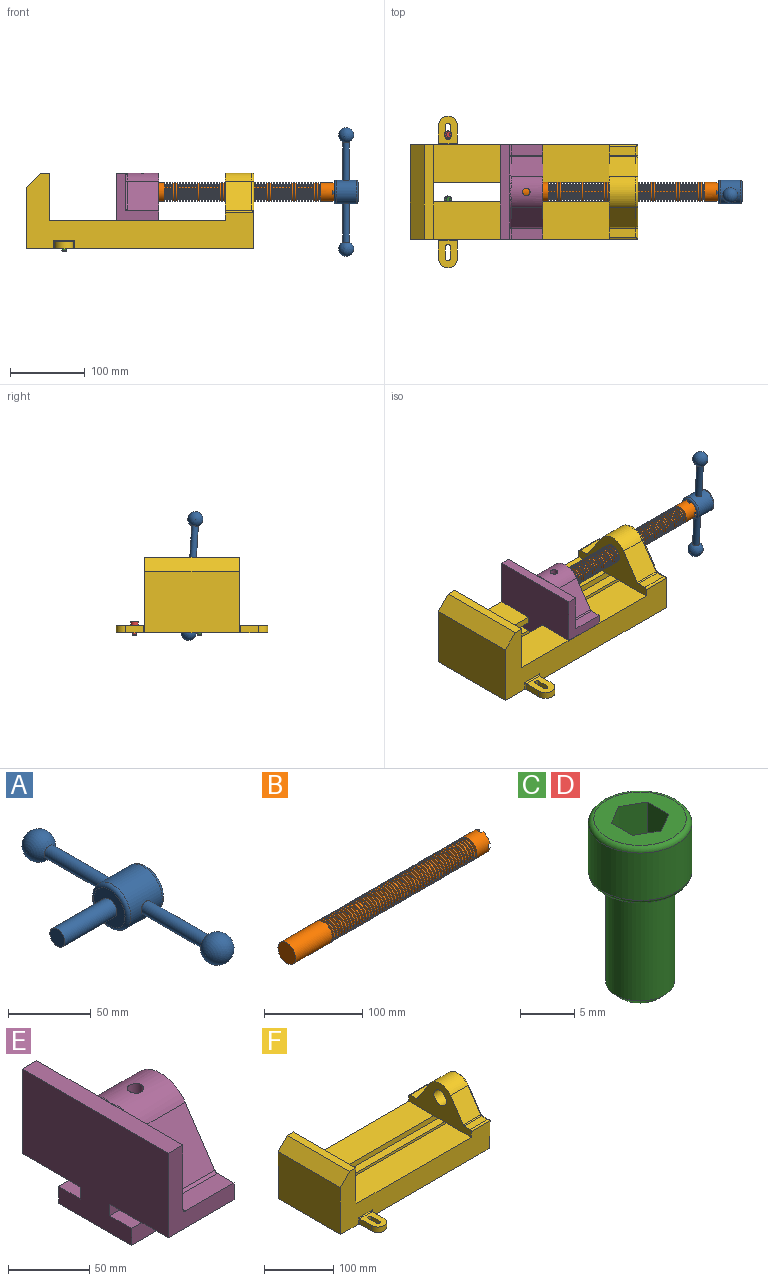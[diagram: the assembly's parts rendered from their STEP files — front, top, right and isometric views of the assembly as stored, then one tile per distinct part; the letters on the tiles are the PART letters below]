
ASSEMBLY  parts=6 mates=7
PART A: 11 faces, bbox 76.2x172.7x34.4 mm
  f0: sphere r=10.16mm, area 1231.8mm2, adj f1
  f1: cylinder r=4.45mm len=51.82mm, axis (0,1,0), area 1438.5mm2, adj f0,f4
  f2: sphere r=10.16mm, area 1231.8mm2, adj f3
  f3: cylinder r=4.45mm len=51.82mm, axis (0,1,0), area 1438.5mm2, adj f2,f4
  f4: cylinder r=15.88mm len=31.75mm, axis (-1,0,0), area 2534.7mm2, adj f1,f3,f9,f10
  f5: cylinder r=6.35mm len=44.45mm, axis (-1,0,0), area 1773.5mm2, adj f6,f8
  f6: plane 12.7x12.7mm, normal (-1,0,0), area 126.7mm2, adj f5
  f7: plane 26.67x26.67mm, normal (1,0,0), area 558.6mm2, adj f10
  f8: plane 26.67x26.67mm, normal (-1,0,0), area 432mm2, adj f5,f9
  f9: torus R=13.33mm, axis (1,0,0), area 374.8mm2, adj f4,f8
  f10: torus R=13.33mm, axis (1,0,0), area 374.8mm2, adj f4,f7
PART B: 220 faces, bbox 279.4x25.4x25.4 mm
  f0: cylinder r=12.7mm len=25.4mm, axis (-1,0,0), area 1468.2mm2, adj f1,f2,f3,f5,f7,f208,f209,f210
  f1: plane 9.9x9.9mm, normal (1,0,0), area 62.3mm2, adj f0,f4,f213,f216
  f2: plane 9.9x9.9mm, normal (1,0,0), area 62.3mm2, adj f0,f4,f210,f218
  f3: plane 9.9x9.9mm, normal (1,0,0), area 62.3mm2, adj f0,f4,f209,f212
  f4: cylinder r=6.35mm len=25.4mm, axis (1,0,0), area 960.3mm2, adj f1,f2,f3,f5,f6,f208,f209,f210
  f5: plane 9.9x9.9mm, normal (1,0,0), area 62.3mm2, adj f0,f4,f215,f217
  f6: plane 12.7x12.7mm, normal (1,0,0), area 126.7mm2, adj f4
  f7: cone r=12.7mm half-angle=76deg, axis (1,0,0), area 188mm2, adj f0,f9
  f8: cone r=10.16mm half-angle=76deg, axis (-1,0,0), area 188mm2, adj f9,f10
  f9: cylinder r=10.16mm len=20.32mm, axis (1,0,0), area 81.1mm2, adj f7,f8
  f10: cylinder r=12.7mm len=25.4mm, axis (-1,0,0), area 131.7mm2, adj f8,f11
  f11: cone r=12.7mm half-angle=76deg, axis (1,0,0), area 188mm2, adj f10,f13
  f12: cone r=10.16mm half-angle=76deg, axis (-1,0,0), area 188mm2, adj f13,f14
  f13: cylinder r=10.16mm len=20.32mm, axis (1,0,0), area 81.1mm2, adj f11,f12
  f14: cylinder r=12.7mm len=25.4mm, axis (-1,0,0), area 131.7mm2, adj f12,f15
  f15: cone r=12.7mm half-angle=76deg, axis (1,0,0), area 188mm2, adj f14,f17
  f16: cone r=10.16mm half-angle=76deg, axis (-1,0,0), area 188mm2, adj f17,f18
  f17: cylinder r=10.16mm len=20.32mm, axis (1,0,0), area 81.1mm2, adj f15,f16
  f18: cylinder r=12.7mm len=25.4mm, axis (-1,0,0), area 131.7mm2, adj f16,f19
  f19: cone r=12.7mm half-angle=76deg, axis (1,0,0), area 188mm2, adj f18,f21
  f20: cone r=10.16mm half-angle=76deg, axis (-1,0,0), area 188mm2, adj f21,f22
  f21: cylinder r=10.16mm len=20.32mm, axis (1,0,0), area 81.1mm2, adj f19,f20
  f22: cylinder r=12.7mm len=25.4mm, axis (-1,0,0), area 131.7mm2, adj f20,f23
  f23: cone r=12.7mm half-angle=76deg, axis (1,0,0), area 188mm2, adj f22,f25
  f24: cone r=10.16mm half-angle=76deg, axis (-1,0,0), area 188mm2, adj f25,f26
  f25: cylinder r=10.16mm len=20.32mm, axis (1,0,0), area 81.1mm2, adj f23,f24
  f26: cylinder r=12.7mm len=25.4mm, axis (-1,0,0), area 131.7mm2, adj f24,f27
  f27: cone r=12.7mm half-angle=76deg, axis (1,0,0), area 188mm2, adj f26,f29
  f28: cone r=10.16mm half-angle=76deg, axis (-1,0,0), area 188mm2, adj f29,f30
  f29: cylinder r=10.16mm len=20.32mm, axis (1,0,0), area 81.1mm2, adj f27,f28
  f30: cylinder r=12.7mm len=25.4mm, axis (-1,0,0), area 131.7mm2, adj f28,f31
  f31: cone r=12.7mm half-angle=76deg, axis (1,0,0), area 188mm2, adj f30,f33
  f32: cone r=10.16mm half-angle=76deg, axis (-1,0,0), area 188mm2, adj f33,f34
  f33: cylinder r=10.16mm len=20.32mm, axis (1,0,0), area 81.1mm2, adj f31,f32
  f34: cylinder r=12.7mm len=25.4mm, axis (-1,0,0), area 131.7mm2, adj f32,f35
  f35: cone r=12.7mm half-angle=76deg, axis (1,0,0), area 188mm2, adj f34,f37
  f36: cone r=10.16mm half-angle=76deg, axis (-1,0,0), area 188mm2, adj f37,f38
  f37: cylinder r=10.16mm len=20.32mm, axis (1,0,0), area 81.1mm2, adj f35,f36
  f38: cylinder r=12.7mm len=25.4mm, axis (-1,0,0), area 131.7mm2, adj f36,f39
  f39: cone r=12.7mm half-angle=76deg, axis (1,0,0), area 188mm2, adj f38,f41
  f40: cone r=10.16mm half-angle=76deg, axis (-1,0,0), area 188mm2, adj f41,f42
  f41: cylinder r=10.16mm len=20.32mm, axis (1,0,0), area 81.1mm2, adj f39,f40
  f42: cylinder r=12.7mm len=25.4mm, axis (-1,0,0), area 131.7mm2, adj f40,f43
  f43: cone r=12.7mm half-angle=76deg, axis (1,0,0), area 188mm2, adj f42,f45
  f44: cone r=10.16mm half-angle=76deg, axis (-1,0,0), area 188mm2, adj f45,f46
  f45: cylinder r=10.16mm len=20.32mm, axis (1,0,0), area 81.1mm2, adj f43,f44
  f46: cylinder r=12.7mm len=25.4mm, axis (-1,0,0), area 131.7mm2, adj f44,f47
  f47: cone r=12.7mm half-angle=76deg, axis (1,0,0), area 188mm2, adj f46,f49
  f48: cone r=10.16mm half-angle=76deg, axis (-1,0,0), area 188mm2, adj f49,f50
  f49: cylinder r=10.16mm len=20.32mm, axis (1,0,0), area 81.1mm2, adj f47,f48
  f50: cylinder r=12.7mm len=25.4mm, axis (-1,0,0), area 131.7mm2, adj f48,f51
  f51: cone r=12.7mm half-angle=76deg, axis (1,0,0), area 188mm2, adj f50,f53
  f52: cone r=10.16mm half-angle=76deg, axis (-1,0,0), area 188mm2, adj f53,f54
  f53: cylinder r=10.16mm len=20.32mm, axis (1,0,0), area 81.1mm2, adj f51,f52
  f54: cylinder r=12.7mm len=25.4mm, axis (-1,0,0), area 131.7mm2, adj f52,f55
  f55: cone r=12.7mm half-angle=76deg, axis (1,0,0), area 188mm2, adj f54,f57
  f56: cone r=10.16mm half-angle=76deg, axis (-1,0,0), area 188mm2, adj f57,f58
  f57: cylinder r=10.16mm len=20.32mm, axis (1,0,0), area 81.1mm2, adj f55,f56
  f58: cylinder r=12.7mm len=25.4mm, axis (-1,0,0), area 131.7mm2, adj f56,f59
  f59: cone r=12.7mm half-angle=76deg, axis (1,0,0), area 188mm2, adj f58,f61
  f60: cone r=10.16mm half-angle=76deg, axis (-1,0,0), area 188mm2, adj f61,f62
  f61: cylinder r=10.16mm len=20.32mm, axis (1,0,0), area 81.1mm2, adj f59,f60
  f62: cylinder r=12.7mm len=25.4mm, axis (-1,0,0), area 131.7mm2, adj f60,f63
  f63: cone r=12.7mm half-angle=76deg, axis (1,0,0), area 188mm2, adj f62,f65
  f64: cone r=10.16mm half-angle=76deg, axis (-1,0,0), area 188mm2, adj f65,f66
  f65: cylinder r=10.16mm len=20.32mm, axis (1,0,0), area 81.1mm2, adj f63,f64
  f66: cylinder r=12.7mm len=25.4mm, axis (-1,0,0), area 131.7mm2, adj f64,f67
  f67: cone r=12.7mm half-angle=76deg, axis (1,0,0), area 188mm2, adj f66,f69
  f68: cone r=10.16mm half-angle=76deg, axis (-1,0,0), area 188mm2, adj f69,f70
  f69: cylinder r=10.16mm len=20.32mm, axis (1,0,0), area 81.1mm2, adj f67,f68
  f70: cylinder r=12.7mm len=25.4mm, axis (-1,0,0), area 131.7mm2, adj f68,f71
  f71: cone r=12.7mm half-angle=76deg, axis (1,0,0), area 188mm2, adj f70,f73
  f72: cone r=10.16mm half-angle=76deg, axis (-1,0,0), area 188mm2, adj f73,f74
  f73: cylinder r=10.16mm len=20.32mm, axis (1,0,0), area 81.1mm2, adj f71,f72
  f74: cylinder r=12.7mm len=25.4mm, axis (-1,0,0), area 131.7mm2, adj f72,f75
  f75: cone r=12.7mm half-angle=76deg, axis (1,0,0), area 188mm2, adj f74,f77
  f76: cone r=10.16mm half-angle=76deg, axis (-1,0,0), area 188mm2, adj f77,f78
  f77: cylinder r=10.16mm len=20.32mm, axis (1,0,0), area 81.1mm2, adj f75,f76
  f78: cylinder r=12.7mm len=25.4mm, axis (-1,0,0), area 131.7mm2, adj f76,f79
  f79: cone r=12.7mm half-angle=76deg, axis (1,0,0), area 188mm2, adj f78,f81
  f80: cone r=10.16mm half-angle=76deg, axis (-1,0,0), area 188mm2, adj f81,f82
  f81: cylinder r=10.16mm len=20.32mm, axis (1,0,0), area 81.1mm2, adj f79,f80
  f82: cylinder r=12.7mm len=25.4mm, axis (-1,0,0), area 131.7mm2, adj f80,f83
  f83: cone r=12.7mm half-angle=76deg, axis (1,0,0), area 188mm2, adj f82,f85
  f84: cone r=10.16mm half-angle=76deg, axis (-1,0,0), area 188mm2, adj f85,f86
  f85: cylinder r=10.16mm len=20.32mm, axis (1,0,0), area 81.1mm2, adj f83,f84
  f86: cylinder r=12.7mm len=25.4mm, axis (-1,0,0), area 131.7mm2, adj f84,f87
  f87: cone r=12.7mm half-angle=76deg, axis (1,0,0), area 188mm2, adj f86,f89
  f88: cone r=10.16mm half-angle=76deg, axis (-1,0,0), area 188mm2, adj f89,f90
  f89: cylinder r=10.16mm len=20.32mm, axis (1,0,0), area 81.1mm2, adj f87,f88
  f90: cylinder r=12.7mm len=25.4mm, axis (-1,0,0), area 131.7mm2, adj f88,f91
  f91: cone r=12.7mm half-angle=76deg, axis (1,0,0), area 188mm2, adj f90,f93
  f92: cone r=10.16mm half-angle=76deg, axis (-1,0,0), area 188mm2, adj f93,f94
  f93: cylinder r=10.16mm len=20.32mm, axis (1,0,0), area 81.1mm2, adj f91,f92
  f94: cylinder r=12.7mm len=25.4mm, axis (-1,0,0), area 131.7mm2, adj f92,f95
  f95: cone r=12.7mm half-angle=76deg, axis (1,0,0), area 188mm2, adj f94,f97
  f96: cone r=10.16mm half-angle=76deg, axis (-1,0,0), area 188mm2, adj f97,f98
  f97: cylinder r=10.16mm len=20.32mm, axis (1,0,0), area 81.1mm2, adj f95,f96
  f98: cylinder r=12.7mm len=25.4mm, axis (-1,0,0), area 131.7mm2, adj f96,f99
  f99: cone r=12.7mm half-angle=76deg, axis (1,0,0), area 188mm2, adj f98,f101
  f100: cone r=10.16mm half-angle=76deg, axis (-1,0,0), area 188mm2, adj f101,f102
  f101: cylinder r=10.16mm len=20.32mm, axis (1,0,0), area 81.1mm2, adj f99,f100
  f102: cylinder r=12.7mm len=25.4mm, axis (-1,0,0), area 131.7mm2, adj f100,f103
  f103: cone r=12.7mm half-angle=76deg, axis (1,0,0), area 188mm2, adj f102,f105
  f104: cone r=10.16mm half-angle=76deg, axis (-1,0,0), area 188mm2, adj f105,f106
  f105: cylinder r=10.16mm len=20.32mm, axis (1,0,0), area 81.1mm2, adj f103,f104
  f106: cylinder r=12.7mm len=25.4mm, axis (-1,0,0), area 131.7mm2, adj f104,f107
  f107: cone r=12.7mm half-angle=76deg, axis (1,0,0), area 188mm2, adj f106,f109
  f108: cone r=10.16mm half-angle=76deg, axis (-1,0,0), area 188mm2, adj f109,f110
  f109: cylinder r=10.16mm len=20.32mm, axis (1,0,0), area 81.1mm2, adj f107,f108
  f110: cylinder r=12.7mm len=25.4mm, axis (-1,0,0), area 131.7mm2, adj f108,f111
  f111: cone r=12.7mm half-angle=76deg, axis (1,0,0), area 188mm2, adj f110,f113
  f112: cone r=10.16mm half-angle=76deg, axis (-1,0,0), area 188mm2, adj f113,f114
  f113: cylinder r=10.16mm len=20.32mm, axis (1,0,0), area 81.1mm2, adj f111,f112
  f114: cylinder r=12.7mm len=25.4mm, axis (-1,0,0), area 131.7mm2, adj f112,f115
  f115: cone r=12.7mm half-angle=76deg, axis (1,0,0), area 188mm2, adj f114,f117
  f116: cone r=10.16mm half-angle=76deg, axis (-1,0,0), area 188mm2, adj f117,f118
  f117: cylinder r=10.16mm len=20.32mm, axis (1,0,0), area 81.1mm2, adj f115,f116
  f118: cylinder r=12.7mm len=25.4mm, axis (-1,0,0), area 131.7mm2, adj f116,f119
  f119: cone r=12.7mm half-angle=76deg, axis (1,0,0), area 188mm2, adj f118,f121
  f120: cone r=10.16mm half-angle=76deg, axis (-1,0,0), area 188mm2, adj f121,f122
  f121: cylinder r=10.16mm len=20.32mm, axis (1,0,0), area 81.1mm2, adj f119,f120
  f122: cylinder r=12.7mm len=25.4mm, axis (-1,0,0), area 131.7mm2, adj f120,f123
  f123: cone r=12.7mm half-angle=76deg, axis (1,0,0), area 188mm2, adj f122,f125
  f124: cone r=10.16mm half-angle=76deg, axis (-1,0,0), area 188mm2, adj f125,f126
  f125: cylinder r=10.16mm len=20.32mm, axis (1,0,0), area 81.1mm2, adj f123,f124
  f126: cylinder r=12.7mm len=25.4mm, axis (-1,0,0), area 131.7mm2, adj f124,f127
  f127: cone r=12.7mm half-angle=76deg, axis (1,0,0), area 188mm2, adj f126,f129
  f128: cone r=10.16mm half-angle=76deg, axis (-1,0,0), area 188mm2, adj f129,f130
  f129: cylinder r=10.16mm len=20.32mm, axis (1,0,0), area 81.1mm2, adj f127,f128
  f130: cylinder r=12.7mm len=25.4mm, axis (-1,0,0), area 131.7mm2, adj f128,f131
  f131: cone r=12.7mm half-angle=76deg, axis (1,0,0), area 188mm2, adj f130,f133
  f132: cone r=10.16mm half-angle=76deg, axis (-1,0,0), area 188mm2, adj f133,f134
  f133: cylinder r=10.16mm len=20.32mm, axis (1,0,0), area 81.1mm2, adj f131,f132
  f134: cylinder r=12.7mm len=25.4mm, axis (-1,0,0), area 131.7mm2, adj f132,f135
  f135: cone r=12.7mm half-angle=76deg, axis (1,0,0), area 188mm2, adj f134,f137
  f136: cone r=10.16mm half-angle=76deg, axis (-1,0,0), area 188mm2, adj f137,f138
  f137: cylinder r=10.16mm len=20.32mm, axis (1,0,0), area 81.1mm2, adj f135,f136
  f138: cylinder r=12.7mm len=25.4mm, axis (-1,0,0), area 131.7mm2, adj f136,f139
  f139: cone r=12.7mm half-angle=76deg, axis (1,0,0), area 188mm2, adj f138,f141
  f140: cone r=10.16mm half-angle=76deg, axis (-1,0,0), area 188mm2, adj f141,f142
  f141: cylinder r=10.16mm len=20.32mm, axis (1,0,0), area 81.1mm2, adj f139,f140
  f142: cylinder r=12.7mm len=25.4mm, axis (-1,0,0), area 131.7mm2, adj f140,f143
  f143: cone r=12.7mm half-angle=76deg, axis (1,0,0), area 188mm2, adj f142,f145
  f144: cone r=10.16mm half-angle=76deg, axis (-1,0,0), area 188mm2, adj f145,f146
  f145: cylinder r=10.16mm len=20.32mm, axis (1,0,0), area 81.1mm2, adj f143,f144
  f146: cylinder r=12.7mm len=25.4mm, axis (-1,0,0), area 131.7mm2, adj f144,f147
  f147: cone r=12.7mm half-angle=76deg, axis (1,0,0), area 188mm2, adj f146,f149
  f148: cone r=10.16mm half-angle=76deg, axis (-1,0,0), area 188mm2, adj f149,f150
  f149: cylinder r=10.16mm len=20.32mm, axis (1,0,0), area 81.1mm2, adj f147,f148
  f150: cylinder r=12.7mm len=25.4mm, axis (-1,0,0), area 131.7mm2, adj f148,f151
  f151: cone r=12.7mm half-angle=76deg, axis (1,0,0), area 188mm2, adj f150,f153
  f152: cone r=10.16mm half-angle=76deg, axis (-1,0,0), area 188mm2, adj f153,f154
  f153: cylinder r=10.16mm len=20.32mm, axis (1,0,0), area 81.1mm2, adj f151,f152
  f154: cylinder r=12.7mm len=25.4mm, axis (-1,0,0), area 131.7mm2, adj f152,f155
  f155: cone r=12.7mm half-angle=76deg, axis (1,0,0), area 188mm2, adj f154,f157
  f156: cone r=10.16mm half-angle=76deg, axis (-1,0,0), area 188mm2, adj f157,f158
  f157: cylinder r=10.16mm len=20.32mm, axis (1,0,0), area 81.1mm2, adj f155,f156
  f158: cylinder r=12.7mm len=25.4mm, axis (-1,0,0), area 131.7mm2, adj f156,f159
  f159: cone r=12.7mm half-angle=76deg, axis (1,0,0), area 188mm2, adj f158,f161
  f160: cone r=10.16mm half-angle=76deg, axis (-1,0,0), area 188mm2, adj f161,f162
  f161: cylinder r=10.16mm len=20.32mm, axis (1,0,0), area 81.1mm2, adj f159,f160
  f162: cylinder r=12.7mm len=25.4mm, axis (-1,0,0), area 131.7mm2, adj f160,f163
  f163: cone r=12.7mm half-angle=76deg, axis (1,0,0), area 188mm2, adj f162,f165
  f164: cone r=10.16mm half-angle=76deg, axis (-1,0,0), area 188mm2, adj f165,f166
  f165: cylinder r=10.16mm len=20.32mm, axis (1,0,0), area 81.1mm2, adj f163,f164
  f166: cylinder r=12.7mm len=25.4mm, axis (-1,0,0), area 131.7mm2, adj f164,f167
  f167: cone r=12.7mm half-angle=76deg, axis (1,0,0), area 188mm2, adj f166,f169
  f168: cone r=10.16mm half-angle=76deg, axis (-1,0,0), area 188mm2, adj f169,f170
  f169: cylinder r=10.16mm len=20.32mm, axis (1,0,0), area 81.1mm2, adj f167,f168
  f170: cylinder r=12.7mm len=25.4mm, axis (-1,0,0), area 131.7mm2, adj f168,f171
  f171: cone r=12.7mm half-angle=76deg, axis (1,0,0), area 188mm2, adj f170,f173
  f172: cone r=10.16mm half-angle=76deg, axis (-1,0,0), area 188mm2, adj f173,f174
  f173: cylinder r=10.16mm len=20.32mm, axis (1,0,0), area 81.1mm2, adj f171,f172
  f174: cylinder r=12.7mm len=25.4mm, axis (-1,0,0), area 131.7mm2, adj f172,f175
  f175: cone r=12.7mm half-angle=76deg, axis (1,0,0), area 188mm2, adj f174,f177
  f176: cone r=10.16mm half-angle=76deg, axis (-1,0,0), area 188mm2, adj f177,f178
  f177: cylinder r=10.16mm len=20.32mm, axis (1,0,0), area 81.1mm2, adj f175,f176
  f178: cylinder r=12.7mm len=25.4mm, axis (-1,0,0), area 131.7mm2, adj f176,f179
  f179: cone r=12.7mm half-angle=76deg, axis (1,0,0), area 188mm2, adj f178,f181
  f180: cone r=10.16mm half-angle=76deg, axis (-1,0,0), area 188mm2, adj f181,f182
  f181: cylinder r=10.16mm len=20.32mm, axis (1,0,0), area 81.1mm2, adj f179,f180
  f182: cylinder r=12.7mm len=25.4mm, axis (-1,0,0), area 131.7mm2, adj f180,f183
  f183: cone r=12.7mm half-angle=76deg, axis (1,0,0), area 188mm2, adj f182,f185
  f184: cone r=10.16mm half-angle=76deg, axis (-1,0,0), area 188mm2, adj f185,f186
  f185: cylinder r=10.16mm len=20.32mm, axis (1,0,0), area 81.1mm2, adj f183,f184
  f186: cylinder r=12.7mm len=25.4mm, axis (-1,0,0), area 131.7mm2, adj f184,f187
  f187: cone r=12.7mm half-angle=76deg, axis (1,0,0), area 188mm2, adj f186,f189
  f188: cone r=10.16mm half-angle=76deg, axis (-1,0,0), area 188mm2, adj f189,f190
  f189: cylinder r=10.16mm len=20.32mm, axis (1,0,0), area 81.1mm2, adj f187,f188
  f190: cylinder r=12.7mm len=25.4mm, axis (-1,0,0), area 131.7mm2, adj f188,f191
  f191: cone r=12.7mm half-angle=76deg, axis (1,0,0), area 188mm2, adj f190,f193
  f192: cone r=10.16mm half-angle=76deg, axis (-1,0,0), area 188mm2, adj f193,f194
  f193: cylinder r=10.16mm len=20.32mm, axis (1,0,0), area 81.1mm2, adj f191,f192
  f194: cylinder r=12.7mm len=25.4mm, axis (-1,0,0), area 131.7mm2, adj f192,f195
  f195: cone r=12.7mm half-angle=76deg, axis (1,0,0), area 188mm2, adj f194,f197
  f196: cone r=10.16mm half-angle=76deg, axis (-1,0,0), area 188mm2, adj f197,f198
  f197: cylinder r=10.16mm len=20.32mm, axis (1,0,0), area 81.1mm2, adj f195,f196
  f198: cylinder r=12.7mm len=25.4mm, axis (-1,0,0), area 131.7mm2, adj f196,f199
  f199: cone r=12.7mm half-angle=76deg, axis (1,0,0), area 188mm2, adj f198,f201
  f200: cone r=10.16mm half-angle=76deg, axis (-1,0,0), area 188mm2, adj f201,f202
  f201: cylinder r=10.16mm len=20.32mm, axis (1,0,0), area 81.1mm2, adj f199,f200
  f202: cylinder r=12.7mm len=25.4mm, axis (-1,0,0), area 131.7mm2, adj f200,f203
  f203: cone r=12.7mm half-angle=76deg, axis (1,0,0), area 188mm2, adj f202,f205
  f204: cone r=10.16mm half-angle=76deg, axis (-1,0,0), area 188mm2, adj f205,f207
  f205: cylinder r=10.16mm len=20.32mm, axis (1,0,0), area 81.1mm2, adj f203,f204
  f206: plane 25.4x25.4mm, normal (-1,0,0), area 506.7mm2, adj f207
  f207: cylinder r=12.7mm len=52.45mm, axis (-1,0,0), area 4185.4mm2, adj f204,f206
  f208: plane 6.88x5.08mm, normal (1,0,0), area 32.7mm2, adj f0,f4,f209,f210
  f209: plane 6.62x2.54mm, normal (0,-1,0), area 16.8mm2, adj f0,f3,f4,f208
  f210: plane 6.62x2.54mm, normal (0,1,0), area 16.8mm2, adj f0,f2,f4,f208
  f211: plane 6.88x5.08mm, normal (1,0,0), area 32.7mm2, adj f0,f4,f212,f213
  f212: plane 6.62x2.54mm, normal (0,0,1), area 16.8mm2, adj f0,f3,f4,f211
  f213: plane 6.62x2.54mm, normal (0,0,-1), area 16.8mm2, adj f0,f1,f4,f211
  f214: plane 6.88x5.08mm, normal (1,0,0), area 32.7mm2, adj f0,f4,f215,f216
  f215: plane 6.62x2.54mm, normal (0,1,0), area 16.8mm2, adj f0,f4,f5,f214
  f216: plane 6.62x2.54mm, normal (0,-1,0), area 16.8mm2, adj f0,f1,f4,f214
  f217: plane 6.62x2.54mm, normal (0,0,-1), area 16.8mm2, adj f0,f4,f5,f219
  f218: plane 6.62x2.54mm, normal (0,0,1), area 16.8mm2, adj f0,f2,f4,f219
  f219: plane 6.88x5.08mm, normal (1,0,0), area 32.7mm2, adj f0,f4,f217,f218
PART C: 15 faces, bbox 10.3x10.3x19.1 mm
  f0: plane 8.51x8.51mm, normal (0,0,1), area 37.2mm2, adj f5,f6,f7,f8,f9,f10,f14
  f1: cylinder r=3.17mm len=11.94mm, axis (0,0,1), area 238.2mm2, adj f4,f12
  f2: plane 4.83x4.83mm, normal (0,0,-1), area 18.3mm2, adj f12
  f3: cylinder r=4.76mm len=9.53mm, axis (0,0,-1), area 159.6mm2, adj f13,f14
  f4: plane 8.51x8.51mm, normal (0,0,-1), area 25.2mm2, adj f1,f13
  f5: plane 4.83x2.38mm, normal (-0.5,-0.87,0), area 13.3mm2, adj f0,f6,f10,f11
  f6: plane 4.83x2.38mm, normal (0.5,-0.87,0), area 13.3mm2, adj f0,f5,f7,f11
  f7: plane 4.83x2.75mm, normal (1,0,0), area 13.3mm2, adj f0,f6,f8,f11
  f8: plane 4.83x2.38mm, normal (0.5,0.87,0), area 13.3mm2, adj f0,f7,f9,f11
  f9: plane 4.83x2.38mm, normal (-0.5,0.87,0), area 13.3mm2, adj f0,f8,f10,f11
  f10: plane 4.83x2.75mm, normal (-1,0,0), area 13.3mm2, adj f0,f5,f9,f11
  f11: plane 5.5x4.76mm, normal (0,0,1), area 19.6mm2, adj f5,f6,f7,f8,f9,f10
  f12: cone r=3.17mm half-angle=45deg, axis (0,0,1), area 18.9mm2, adj f1,f2
  f13: torus R=4.25mm, axis (0,0,1), area 23mm2, adj f3,f4
  f14: torus R=4.25mm, axis (0,0,1), area 23mm2, adj f0,f3
PART D: same geometry as C
PART E: 36 faces, bbox 57.2x127x89 mm
  f0: plane 57.15x50.8mm, normal (0,0,-1), area 2903.2mm2, adj f6,f9,f10,f23
  f1: cylinder r=12.7mm len=44.45mm, axis (1,0,0), area 3464.3mm2, adj f6,f15,f16
  f2: plane 41.91x14.52mm, normal (0,0,1), area 608.5mm2, adj f6,f11,f24,f25
  f3: plane 51.86x48.26mm, normal (1,0,0), area 1495.7mm2, adj f8,f10,f31,f33,f35
  f4: plane 51.86x48.26mm, normal (1,0,0), area 1495.7mm2, adj f8,f11,f24,f28,f29
  f5: plane 57.15x50.8mm, normal (0,0,-1), area 2903.2mm2, adj f6,f9,f11,f22
  f6: plane 127x85.09mm, normal (1,0,0), area 5190.6mm2, adj f0,f1,f2,f5,f7,f10,f11,f12
  f7: plane 41.91x14.52mm, normal (0,0,1), area 608.5mm2, adj f6,f10,f30,f31
  f8: plane 127x12.7mm, normal (0,0,1), area 1612.9mm2, adj f3,f4,f9,f10,f11,f26,f34
  f9: plane 127x85.09mm, normal (-1,0,0), area 9096.8mm2, adj f0,f5,f8,f10,f11,f17,f18,f19
  f10: plane 63.5x57.15mm, normal (0,-1,0), area 1372.3mm2, adj f0,f3,f6,f7,f8,f9,f31
  f11: plane 63.5x57.15mm, normal (0,1,0), area 1372.3mm2, adj f2,f4,f5,f6,f8,f9,f24
  f12: plane 41.91x38.43mm, normal (0,-0.83,0.56), area 1939.2mm2, adj f6,f13,f30,f33
  f13: cylinder r=25.4mm len=44.45mm, axis (1,0,0), area 2026.5mm2, adj f6,f12,f14,f16,f26,f28,f34,f35
  f14: plane 41.91x38.43mm, normal (0,0.83,0.56), area 1939.2mm2, adj f6,f13,f25,f29
  f15: plane 25.4x25.4mm, normal (1,0,0), area 506.7mm2, adj f1
  f16: cylinder r=5.08mm len=13.76mm, axis (0,0,1), area 414mm2, adj f1,f13
  f17: plane 57.15x19.05mm, normal (0,0,1), area 1088.7mm2, adj f6,f9,f18,f23
  f18: plane 57.15x12.7mm, normal (0,-1,0), area 725.8mm2, adj f6,f9,f17,f19
  f19: plane 63.5x57.15mm, normal (0,0,-1), area 3629mm2, adj f6,f9,f18,f20
  f20: plane 57.15x12.7mm, normal (0,1,0), area 725.8mm2, adj f6,f9,f19,f21
  f21: plane 57.15x19.05mm, normal (0,0,1), area 1088.7mm2, adj f6,f9,f20,f22
  f22: plane 57.15x8.89mm, normal (0,1,0), area 508.1mm2, adj f5,f6,f9,f21
  f23: plane 57.15x8.89mm, normal (0,-1,0), area 508.1mm2, adj f0,f6,f9,f17
  f24: cylinder r=2.54mm len=14.52mm, axis (0,-1,0), area 57.9mm2, adj f2,f4,f11,f27
  f25: cylinder r=2.54mm len=41.91mm, axis (1,0,0), area 104.3mm2, adj f2,f6,f14,f27
  f26: bspline ~12.24x2.8mm, area 20.9mm2, adj f8,f13,f28
  f27: sphere r=2.54mm, area 6.3mm2, adj f24,f25,f29
  f28: torus R=27.94mm, axis (1,0,0), area 57.8mm2, adj f4,f13,f26,f29
  f29: cylinder r=2.54mm len=39.84mm, axis (0,-0.56,0.83), area 184.6mm2, adj f4,f14,f27,f28
  f30: cylinder r=2.54mm len=41.91mm, axis (1,0,0), area 104.3mm2, adj f6,f7,f12,f32
  f31: cylinder r=2.54mm len=14.52mm, axis (0,-1,0), area 57.9mm2, adj f3,f7,f10,f32
  f32: sphere r=2.54mm, area 6.3mm2, adj f30,f31,f33
  f33: cylinder r=2.54mm len=39.84mm, axis (0,-0.56,-0.83), area 184.6mm2, adj f3,f12,f32,f35
  f34: bspline ~12.24x2.8mm, area 20.9mm2, adj f8,f13,f35
  f35: torus R=27.94mm, axis (1,0,0), area 57.8mm2, adj f3,f13,f33,f34
PART F: 61 faces, bbox 304.8x203.2x103.7 mm
  f0: plane 304.8x101.6mm, normal (0,1,0), area 13520.3mm2, adj f3,f4,f5,f6,f7,f8,f9,f16
  f1: plane 304.8x101.6mm, normal (0,-1,0), area 13520.3mm2, adj f2,f3,f5,f6,f7,f8,f9,f16
  f2: plane 234.95x50.8mm, normal (0,0,1), area 11935.5mm2, adj f1,f5,f16,f26
  f3: plane 127x99.06mm, normal (1,0,0), area 7097.5mm2, adj f0,f1,f9,f14,f17,f18,f19,f20
  f4: plane 234.95x50.8mm, normal (0,0,1), area 11935.5mm2, adj f0,f5,f16,f27
  f5: plane 127x101.6mm, normal (1,0,0), area 9516.1mm2, adj f0,f1,f2,f4,f6,f9,f18,f19
  f6: plane 127x12.7mm, normal (0,0,1), area 1612.9mm2, adj f0,f1,f5,f7
  f7: plane 127x19.05mm, normal (-0.71,0,0.71), area 3421.5mm2, adj f0,f1,f6,f8
  f8: plane 127x82.55mm, normal (-1,0,0), area 10483.8mm2, adj f0,f1,f7,f9
  f9: plane 304.8x203.2mm, normal (0,0,-1), area 33298.3mm2, adj f0,f1,f3,f5,f8,f21,f22,f39
  f10: plane 35.56x11.98mm, normal (0,0,1), area 426mm2, adj f16,f28,f29,f30
  f11: plane 38.43x35.56mm, normal (0,0.83,0.56), area 1645.4mm2, adj f12,f16,f29,f32
  f12: cylinder r=25.4mm len=42.19mm, axis (1,0,0), area 1770.2mm2, adj f11,f13,f16,f33
  f13: plane 38.43x35.56mm, normal (0,-0.83,0.56), area 1645.4mm2, adj f12,f16,f34,f35
  f14: cylinder r=12.7mm len=38.1mm, axis (1,0,0), area 3040.2mm2, adj f3,f16
  f15: plane 35.56x11.98mm, normal (0,0,1), area 426mm2, adj f16,f34,f36,f38
  f16: plane 127x63.5mm, normal (-1,0,0), area 4155.5mm2, adj f0,f1,f2,f4,f10,f11,f12,f13
  f17: plane 38.1x25.4mm, normal (0,0,-1), area 967.7mm2, adj f3,f16,f26,f27
  f18: plane 273.05x19.05mm, normal (0,0,-1), area 5201.6mm2, adj f3,f5,f19,f26
  f19: plane 273.05x12.7mm, normal (0,1,0), area 3467.7mm2, adj f3,f5,f18,f20
  f20: plane 273.05x19.05mm, normal (0,0,1), area 5201.6mm2, adj f3,f5,f19,f21
  f21: plane 273.05x16.51mm, normal (0,1,0), area 4508.1mm2, adj f3,f5,f9,f20
  f22: plane 273.05x16.51mm, normal (0,-1,0), area 4508.1mm2, adj f3,f5,f9,f23
  f23: plane 273.05x19.05mm, normal (0,0,1), area 5201.6mm2, adj f3,f5,f22,f24
  f24: plane 273.05x12.7mm, normal (0,-1,0), area 3467.7mm2, adj f3,f5,f23,f25
  f25: plane 273.05x19.05mm, normal (0,0,-1), area 5201.6mm2, adj f3,f5,f24,f27
  f26: plane 273.05x8.89mm, normal (0,1,0), area 2427.4mm2, adj f2,f3,f5,f17,f18
  f27: plane 273.05x8.89mm, normal (0,-1,0), area 2427.4mm2, adj f3,f4,f5,f17,f25
  f28: cylinder r=2.54mm len=38.1mm, axis (1,0,0), area 148.3mm2, adj f0,f10,f16,f30
  f29: cylinder r=2.54mm len=35.56mm, axis (-1,0,0), area 88.5mm2, adj f10,f11,f16,f31
  f30: cylinder r=2.54mm len=14.52mm, axis (0,1,0), area 54.3mm2, adj f3,f10,f28,f31
  f31: torus R=5.08mm, axis (-1,0,0), area 13.5mm2, adj f3,f29,f30,f32
  f32: cylinder r=2.54mm len=39.84mm, axis (0,0.56,-0.83), area 184.6mm2, adj f3,f11,f31,f33
  f33: torus R=22.86mm, axis (-1,0,0), area 191.4mm2, adj f3,f12,f32,f35
  f34: cylinder r=2.54mm len=35.56mm, axis (-1,0,0), area 88.5mm2, adj f13,f15,f16,f37
  f35: cylinder r=2.54mm len=39.84mm, axis (0,0.56,0.83), area 184.6mm2, adj f3,f13,f33,f37
  f36: cylinder r=2.54mm len=38.1mm, axis (-1,0,0), area 148.3mm2, adj f1,f15,f16,f38
  f37: torus R=5.08mm, axis (-1,0,0), area 13.5mm2, adj f3,f34,f35,f38
  f38: cylinder r=2.54mm len=14.52mm, axis (0,1,0), area 54.3mm2, adj f3,f15,f36,f37
  f39: plane 23.88x9.53mm, normal (-1,0,0), area 227.4mm2, adj f9,f45,f46,f60
  f40: plane 23.88x9.53mm, normal (1,0,0), area 227.4mm2, adj f9,f45,f46,f58
  f41: cylinder r=3.3mm len=9.53mm, axis (0,0,-1), area 98.8mm2, adj f9,f42,f44,f46
  f42: plane 15.62x9.53mm, normal (-1,0,0), area 148.8mm2, adj f9,f41,f43,f46
  f43: cylinder r=3.3mm len=9.53mm, axis (0,0,-1), area 98.8mm2, adj f9,f42,f44,f46
  f44: plane 15.62x9.53mm, normal (1,0,0), area 148.8mm2, adj f9,f41,f43,f46
  f45: cylinder r=12.7mm len=25.4mm, axis (0,0,-1), area 380mm2, adj f9,f39,f40,f46
  f46: plane 36.58x25.4mm, normal (0,0,1), area 722.4mm2, adj f39,f40,f41,f42,f43,f44,f45,f59
  f47: plane 23.88x9.53mm, normal (-1,0,0), area 227.4mm2, adj f9,f53,f54,f56
  f48: plane 23.88x9.53mm, normal (1,0,0), area 227.4mm2, adj f9,f53,f54,f55
  f49: cylinder r=3.3mm len=9.53mm, axis (0,0,-1), area 98.8mm2, adj f9,f50,f52,f54
  f50: plane 15.62x9.53mm, normal (-1,0,0), area 148.8mm2, adj f9,f49,f51,f54
  f51: cylinder r=3.3mm len=9.53mm, axis (0,0,-1), area 98.8mm2, adj f9,f50,f52,f54
  f52: plane 15.62x9.53mm, normal (1,0,0), area 148.8mm2, adj f9,f49,f51,f54
  f53: cylinder r=12.7mm len=25.4mm, axis (0,0,-1), area 380mm2, adj f9,f47,f48,f54
  f54: plane 36.58x25.4mm, normal (0,0,1), area 722.4mm2, adj f47,f48,f49,f50,f51,f52,f53,f57
  f55: cylinder r=1.52mm len=11.05mm, axis (0,0,-1), area 24.1mm2, adj f0,f9,f48,f57
  f56: cylinder r=1.52mm len=11.05mm, axis (0,0,1), area 24.1mm2, adj f0,f9,f47,f57
  f57: cylinder r=1.52mm len=28.45mm, axis (1,0,0), area 63.5mm2, adj f0,f54,f55,f56
  f58: cylinder r=1.52mm len=11.05mm, axis (0,0,1), area 24.1mm2, adj f1,f9,f40,f59
  f59: cylinder r=1.52mm len=28.45mm, axis (-1,0,0), area 63.5mm2, adj f1,f46,f58,f60
  f60: cylinder r=1.52mm len=11.05mm, axis (0,0,-1), area 24.1mm2, adj f1,f9,f39,f59
PLACE A rot(axis=(-1,0,0),86.6deg) t=(28.56,-159.25,46.81)mm
PLACE B rot(axis=(-1,0,0),86.6deg) t=(47.61,-159.25,46.81)mm
PLACE C t=(-295.03,-93.3,-15.3)mm
PLACE D t=(-295.03,-6.3,-15.3)mm
PLACE E t=(47.87,-83.18,-24.83)mm
PLACE F t=(-41.03,-83.18,-24.83)mm fixed
MATE revolute E.f0 <-> F.f2  axis (0,0,-1) through (-196.6,-121.28,13.27)mm
MATE revolute B.f7 <-> E.f28  axis (-1,0,0) through (-212.74,-83.18,51.37)mm
MATE cylindrical B.f7 <-> F.f12  axis (1,0,0) through (-55.52,-83.18,51.37)mm
MATE pin_slot C.f1 <-> F.f41  axis (0,0,1) through (-295.03,-93.3,-15.3)mm
MATE pin_slot D.f1 <-> F.f49  axis (0,0,1) through (-295.03,-6.3,-15.3)mm
MATE pin_slot D.f1 <-> F.f49  axis (0,0,1) through (-295.03,-6.3,-15.3)mm
MATE fastened B.f4 <-> A.f5  axis (1,0,0) through (66.66,-83.18,51.37)mm
